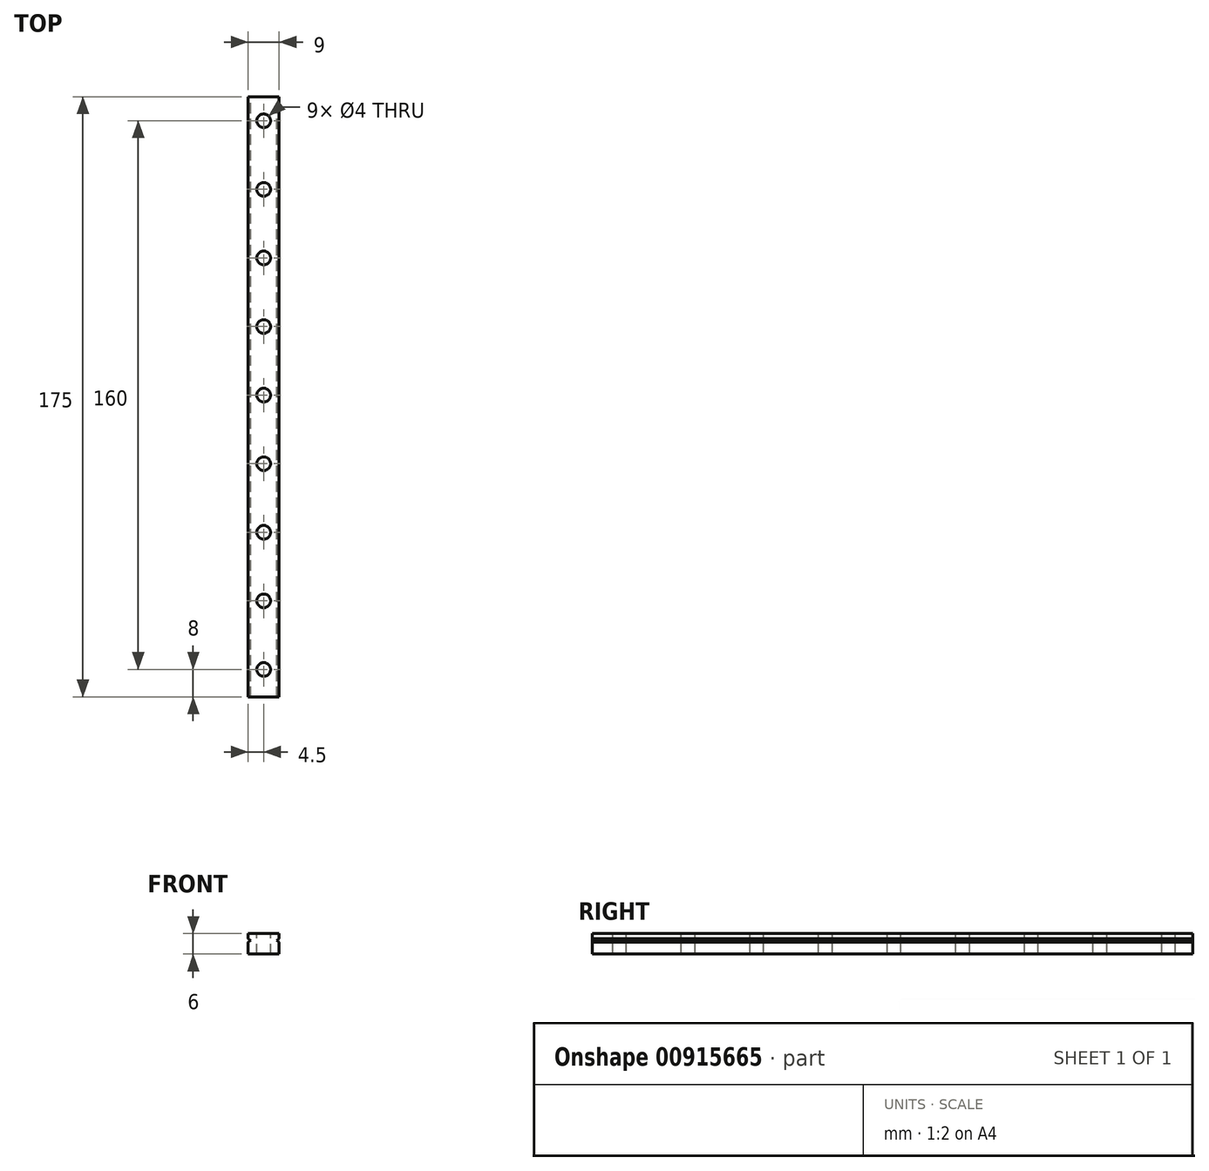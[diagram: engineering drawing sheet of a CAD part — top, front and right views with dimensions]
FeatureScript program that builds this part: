
annotation { "Feature Type Name" : "Feature", "Feature Type Description" : "" }
export const myFeature = defineFeature(function(context is Context, id is Id, definition is map)
    precondition{}
    {
        {
            var Q0;
            Q0=qCreatedBy(makeId("Front.planeOp"),FACE);
            var sketch = newSketch(context, id + "F0", { "sketchPlane" : qUnion([Q0])});
            skLineSegment(sketch, "E0.bottom", {"start": v(-4.5, 6) * mm, "end": v(4.5, 6) * mm});
            skLineSegment(sketch, "E0.top", {"start": v(-4.5, 0) * mm, "end": v(4.5, 0) * mm});
            skLineSegment(sketch, "E0.left", {"start": v(-4.5, 6) * mm, "end": v(-4.5, 4.5) * mm});
            skLineSegment(sketch, "E0.right", {"start": v(4.5, 6) * mm, "end": v(4.5, 4.5) * mm});
            skLineSegment(sketch, "E1", {"start": v(-15.04, 4) * mm, "end": v(13.15, 4) * mm, "construction": true});
            skLineSegment(sketch, "E2", {"start": v(4.5, 4.5) * mm, "end": v(3.8, 4) * mm});
            skLineSegment(sketch, "E3", {"start": v(3.8, 4) * mm, "end": v(4.5, 3.5) * mm});
            skLineSegment(sketch, "E4", {"start": v(-4.5, 4.5) * mm, "end": v(-3.8, 4) * mm});
            skLineSegment(sketch, "E5", {"start": v(-3.8, 4) * mm, "end": v(-4.5, 3.5) * mm});
            skLineSegment(sketch, "E6.trimOffspring", {"start": v(-4.5, 3.5) * mm, "end": v(-4.5, 0) * mm});
            skLineSegment(sketch, "E7.trimOffspring", {"start": v(4.5, 3.5) * mm, "end": v(4.5, 0) * mm});
            skSolve(sketch);
        }
        {
            var Q0;
            Q0 = qSketchRegion(id + "F0", true);
            extrude(context, id + "F1", {"entities" : qUnion([Q0]), "depth" : 175 * mm, "offsetDistance" : 25 * mm});
        }
        {
            var Q0;
            Q0=makeQuery(id+"F1.opExtrude","SWEPT_FACE",FACE,{"disambiguationData":[OSD([sQuery(id+"F0.wireOp",EDGE,"E0.bottom")])]});
            var sketch = newSketch(context, id + "F2", { "sketchPlane" : qUnion([Q0])});
            skCircle(sketch, "E8", {"center": v(0, -7) * mm, "radius": 2 * mm});
            skCircle(sketch, "E9.1.0.0", {"center": v(0, -27) * mm, "radius": 2 * mm});
            skCircle(sketch, "E9.2.0.0", {"center": v(0, -47) * mm, "radius": 2 * mm});
            skCircle(sketch, "E9.3.0.0", {"center": v(0, -67) * mm, "radius": 2 * mm});
            skCircle(sketch, "E9.4.0.0", {"center": v(0, -87) * mm, "radius": 2 * mm});
            skCircle(sketch, "E9.5.0.0", {"center": v(0, -107) * mm, "radius": 2 * mm});
            skCircle(sketch, "E9.6.0.0", {"center": v(0, -127) * mm, "radius": 2 * mm});
            skCircle(sketch, "E9.7.0.0", {"center": v(0, -147) * mm, "radius": 2 * mm});
            skCircle(sketch, "E9.8.0.0", {"center": v(0, -167) * mm, "radius": 2 * mm});
            skLineSegment(sketch, "E9.direction1", {"start": v(0, -7) * mm, "end": v(0, -27) * mm, "construction": true});
            skSolve(sketch);
        }
        {
            var Q0;
            Q0 = qSketchRegion(id + "F2", true);
            extrude(context, id + "F3", {"entities" : qUnion([Q0]), "operationType" : NewBodyOperationType.REMOVE, "endBound" : BoundingType.THROUGH_ALL, "oppositeDirection" : true, "depth" : 25 * mm, "offsetDistance" : 25 * mm});
        }
    });
